# Revit family: Rahmenkassette Schwerlast, blind, RKSL, Nenngröße 350-3, Belastungsklasse 2
name_source: partatom
category: Generic Models
revit_build: Autodesk Revit 2015 (Build: 20140606_1530(x64)
units: mm (PartAtom-declared; Revit-internal decimal feet)

## types (4) — shared parameters
Cut depth = 9 mm  [stored 0.0295276 ft]
Manufacturer = OBO Bettermann
Material = Stainless Steel
URL = http://www.obo-bettermann.com

## per-type parameters (varying)
| type | GTIN | Height | Height 1 | Manufacturer Art.No. | Width | Width 1 |
| RK SL2 V3 20 | 4012195106050 | 20 mm  [stored 0.0656168 ft] | 18 mm  [stored 0.0590551 ft] | 7405952 | 424 mm  [stored 1.39108 ft] | 388 mm  [stored 1.27297 ft] |
| RK SL2 V3 25 | 4012195106067 | 25 mm  [stored 0.082021 ft] | 23 mm  [stored 0.0754593 ft] | 7405956 | 424 mm  [stored 1.39108 ft] | 388 mm  [stored 1.27297 ft] |
| RK SL2 V3 30 | 4012195106074 | 30 mm  [stored 0.0984252 ft] | 28 mm  [stored 0.0918635 ft] | 7405960 | 324 mm  [stored 1.06299 ft] | 288 mm  [stored 0.944882 ft] |
| RK SL2 V3 40 | 4012195106111 | 40 mm  [stored 0.131234 ft] | 38 mm  [stored 0.124672 ft] | 7405968 | 424 mm  [stored 1.39108 ft] | 388 mm  [stored 1.27297 ft] |

note: column(s) folded — value = type name in every type: Article Type

note: [stored X ft] marks values corroborated as IEEE doubles in the binary element streams (Revit-internal decimal feet)

## geometry (parser evidence)
native form markers: Sweep x2
no freeform markers — native parametric forms only
